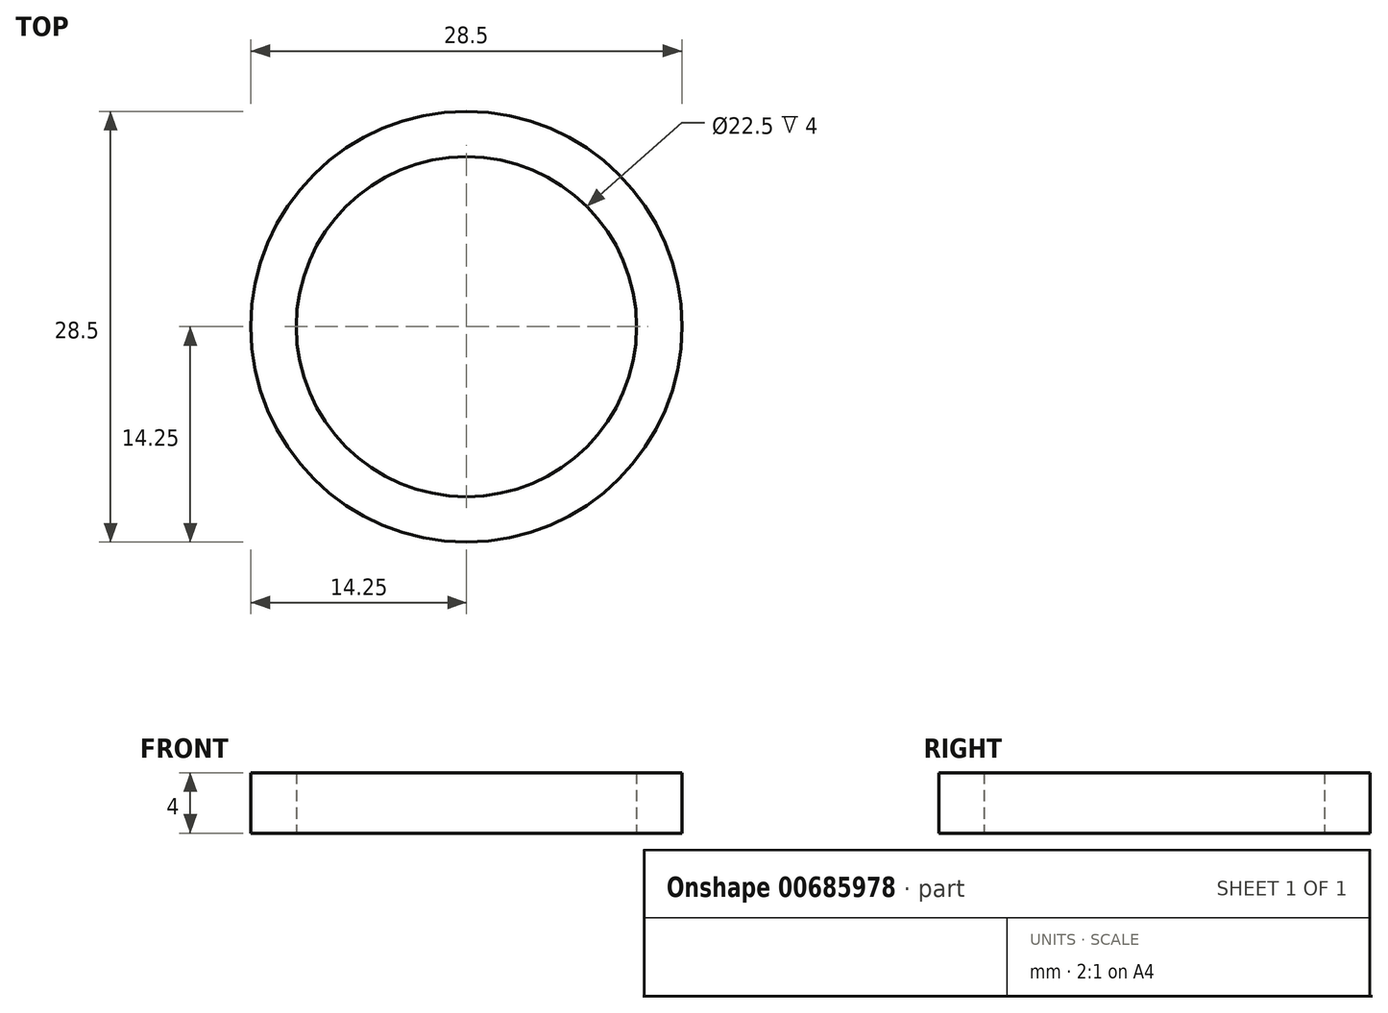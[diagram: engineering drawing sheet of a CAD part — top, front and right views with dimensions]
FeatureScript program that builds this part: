
annotation { "Feature Type Name" : "Feature", "Feature Type Description" : "" }
export const myFeature = defineFeature(function(context is Context, id is Id, definition is map)
    precondition{}
    {
        {
            var Q0;
            Q0=qCreatedBy(makeId("Top.planeOp"),FACE);
            var sketch = newSketch(context, id + "F0", { "sketchPlane" : qUnion([Q0])});
            skCircle(sketch, "E0", {"center": v(0, 0) * mm, "radius": 14.25 * mm});
            skSolve(sketch);
        }
        {
            var Q0;
            Q0=makeQuery(id+"F0.imprint","IMPRINT",FACE,{"disambiguationData":[TD([[makeQuery(id+"F0.imprint","IMPRINT",EDGE,{"derivedFrom":sQuery(id+"F0.wireOp",EDGE,"E0")}),1.0]])]});
            extrude(context, id + "F1", {"entities" : qUnion([Q0]), "depth" : 4 * mm, "offsetDistance" : 25 * mm});
        }
        {
            var Q0;
            Q0=qCreatedBy(makeId("Top.planeOp"),FACE);
            var sketch = newSketch(context, id + "F2", { "sketchPlane" : qUnion([Q0])});
            skCircle(sketch, "E1", {"center": v(0, 0) * mm, "radius": 11.25 * mm});
            skSolve(sketch);
        }
        {
            var Q0;
            Q0 = qSketchRegion(id + "F2", true);
            var Q1;
            Q1=sQuery(id+"F2.wireOp",EDGE,"E1");
            extrude(context, id + "F3", {"entities" : qUnion([Q0]), "operationType" : NewBodyOperationType.REMOVE, "surfaceEntities" : qUnion([Q1]), "depth" : 4 * mm, "offsetDistance" : 25 * mm});
        }
    });
